AUTODESK INVENTOR PART (.ipt)
format: ipt  version: 2024 (Build 280153000, 153)  size: 87,552 bytes
history: native  units: in
note: dims shown in document units (in); Inventor stores cm internally (conversion verified against a paired STEP export)
features: extrude x1, sketch x1
ambient origin geometry x8: Origin, YZ Plane, XZ Plane, XY Plane, X Axis, Y Axis, Z Axis, Center Point
bodies: Solid1 (feature_tree)
feature tree (2):
  extrude  "Extrusion1"  Depth=3.937in
  sketch  "Sketch1"  dims[d0=21.6535in d1=3.937in d7=0.315in d8=0.315in d9=0.315in d10=0.315in d11=5.9055in d12=1.9685in d13=5.9055in d14=5.9055in d15=1.9685in d16=0.748in d17=0.0in]
